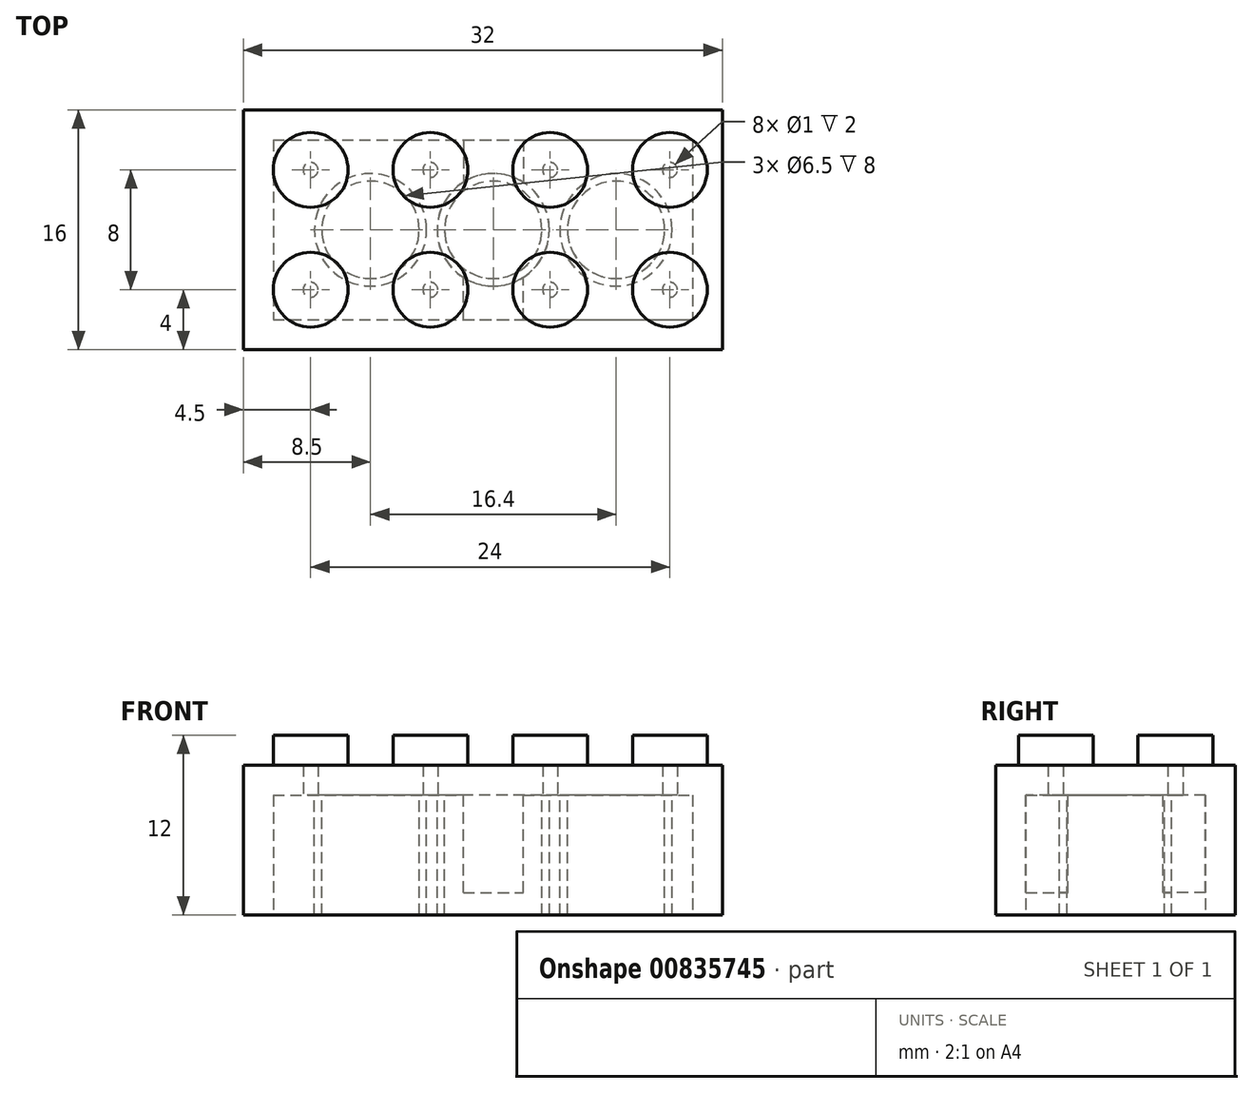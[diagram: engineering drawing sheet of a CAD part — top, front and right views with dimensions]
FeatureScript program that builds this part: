
annotation { "Feature Type Name" : "Feature", "Feature Type Description" : "" }
export const myFeature = defineFeature(function(context is Context, id is Id, definition is map)
    precondition{}
    {
        {
            var Q0;
            Q0=qCreatedBy(makeId("Top.planeOp"),FACE);
            var sketch = newSketch(context, id + "F0", { "sketchPlane" : qUnion([Q0])});
            skLineSegment(sketch, "E0.bottom", {"start": v(-16, 8) * mm, "end": v(16, 8) * mm});
            skLineSegment(sketch, "E0.top", {"start": v(-16, -8) * mm, "end": v(16, -8) * mm});
            skLineSegment(sketch, "E0.left", {"start": v(-16, 8) * mm, "end": v(-16, -8) * mm});
            skLineSegment(sketch, "E0.right", {"start": v(16, 8) * mm, "end": v(16, -8) * mm});
            skPoint(sketch, "E1", {"position": v(-16, 0) * mm});
            skPoint(sketch, "E2", {"position": v(0, 8) * mm});
            skPoint(sketch, "E3", {"position": v(16, 0) * mm});
            skPoint(sketch, "E4", {"position": v(0, -8) * mm});
            skPoint(sketch, "E5", {"position": v(0, 0) * mm});
            skSolve(sketch);
        }
        {
            var Q0;
            Q0=makeQuery(id+"F0.imprint","IMPRINT",FACE,{"disambiguationData":[TD([[makeQuery(id+"F0.imprint","IMPRINT",EDGE,{"derivedFrom":sQuery(id+"F0.wireOp",EDGE,"E0.bottom")}),-1.0]])]});
            extrude(context, id + "F1", {"entities" : qUnion([Q0]), "depth" : 10 * mm, "offsetDistance" : 25 * mm});
        }
        {
            var Q0;
            Q0=makeQuery(id+"F1.opExtrude","CAP_FACE",FACE,{"disambiguationData":[OSD([sQuery(id+"F0.wireOp",EDGE,"E0.bottom"),sQuery(id+"F0.wireOp",EDGE,"E0.top"),sQuery(id+"F0.wireOp",EDGE,"E0.left"),sQuery(id+"F0.wireOp",EDGE,"E0.right")])],"isStart":false});
            var sketch = newSketch(context, id + "F2", { "sketchPlane" : qUnion([Q0])});
            skCircle(sketch, "E6", {"center": v(-11.5, 4) * mm, "radius": 2.5 * mm});
            skCircle(sketch, "E7.0.1.0", {"center": v(-11.5, -4) * mm, "radius": 2.5 * mm});
            skCircle(sketch, "E7.1.0.0", {"center": v(-3.5, 4) * mm, "radius": 2.5 * mm});
            skCircle(sketch, "E7.1.1.0", {"center": v(-3.5, -4) * mm, "radius": 2.5 * mm});
            skCircle(sketch, "E7.2.0.0", {"center": v(4.5, 4) * mm, "radius": 2.5 * mm});
            skCircle(sketch, "E7.2.1.0", {"center": v(4.5, -4) * mm, "radius": 2.5 * mm});
            skCircle(sketch, "E7.3.0.0", {"center": v(12.5, 4) * mm, "radius": 2.5 * mm});
            skCircle(sketch, "E7.3.1.0", {"center": v(12.5, -4) * mm, "radius": 2.5 * mm});
            skLineSegment(sketch, "E7.direction1", {"start": v(-11.5, 4) * mm, "end": v(-3.5, 4) * mm, "construction": true});
            skLineSegment(sketch, "E7.direction2", {"start": v(-11.5, 4) * mm, "end": v(-11.5, -4) * mm, "construction": true});
            skSolve(sketch);
        }
        {
            var Q0;
            Q0=makeQuery(id+"F2.imprint","IMPRINT",FACE,{"disambiguationData":[TD([[makeQuery(id+"F2.imprint","IMPRINT",EDGE,{"derivedFrom":sQuery(id+"F2.wireOp",EDGE,"E6")}),1.0]])]});
            var Q1;
            Q1=makeQuery(id+"F2.imprint","IMPRINT",FACE,{"disambiguationData":[TD([[makeQuery(id+"F2.imprint","IMPRINT",EDGE,{"derivedFrom":sQuery(id+"F2.wireOp",EDGE,"E7.1.0.0")}),1.0]])]});
            var Q2;
            Q2=makeQuery(id+"F2.imprint","IMPRINT",FACE,{"disambiguationData":[TD([[makeQuery(id+"F2.imprint","IMPRINT",EDGE,{"derivedFrom":sQuery(id+"F2.wireOp",EDGE,"E7.3.0.0")}),1.0]])]});
            var Q3;
            Q3=makeQuery(id+"F2.imprint","IMPRINT",FACE,{"disambiguationData":[TD([[makeQuery(id+"F2.imprint","IMPRINT",EDGE,{"derivedFrom":sQuery(id+"F2.wireOp",EDGE,"E7.3.1.0")}),1.0]])]});
            var Q4;
            Q4=makeQuery(id+"F2.imprint","IMPRINT",FACE,{"disambiguationData":[TD([[makeQuery(id+"F2.imprint","IMPRINT",EDGE,{"derivedFrom":sQuery(id+"F2.wireOp",EDGE,"E7.2.1.0")}),1.0]])]});
            var Q5;
            Q5=makeQuery(id+"F2.imprint","IMPRINT",FACE,{"disambiguationData":[TD([[makeQuery(id+"F2.imprint","IMPRINT",EDGE,{"derivedFrom":sQuery(id+"F2.wireOp",EDGE,"E7.1.1.0")}),1.0]])]});
            var Q6;
            Q6=makeQuery(id+"F2.imprint","IMPRINT",FACE,{"disambiguationData":[TD([[makeQuery(id+"F2.imprint","IMPRINT",EDGE,{"derivedFrom":sQuery(id+"F2.wireOp",EDGE,"E7.0.1.0")}),1.0]])]});
            var Q7;
            Q7=makeQuery(id+"F2.imprint","IMPRINT",FACE,{"disambiguationData":[TD([[makeQuery(id+"F2.imprint","IMPRINT",EDGE,{"derivedFrom":sQuery(id+"F2.wireOp",EDGE,"E7.2.0.0")}),1.0]])]});
            extrude(context, id + "F3", {"entities" : qUnion([Q0, Q1, Q2, Q3, Q4, Q5, Q6, Q7]), "operationType" : NewBodyOperationType.ADD, "depth" : 2 * mm, "offsetDistance" : 25 * mm});
        }
        {
            var Q0;
            Q0=makeQuery(id+"F1.opExtrude","CAP_FACE",FACE,{"disambiguationData":[OSD([sQuery(id+"F0.wireOp",EDGE,"E0.bottom"),sQuery(id+"F0.wireOp",EDGE,"E0.top"),sQuery(id+"F0.wireOp",EDGE,"E0.left"),sQuery(id+"F0.wireOp",EDGE,"E0.right")])],"isStart":true});
            shell(context, id + "F4", {"entities" : qUnion([Q0]), "thickness" : 2 * mm});
        }
        {
            var Q0;
            Q0=makeQuery(id+"F4.opShell","OFFSET_FACE",FACE,{"disambiguationData":[OSD([sQuery(id+"F0.wireOp",EDGE,"E0.bottom"),sQuery(id+"F0.wireOp",EDGE,"E0.top"),sQuery(id+"F0.wireOp",EDGE,"E0.left"),sQuery(id+"F0.wireOp",EDGE,"E0.right")])]});
            var sketch = newSketch(context, id + "F5", { "sketchPlane" : qUnion([Q0])});
            skCircle(sketch, "E8", {"center": v(-7.5, 0) * mm, "radius": 3.75 * mm});
            skLineSegment(sketch, "E9", {"start": v(-11.5, 4) * mm, "end": v(-11.5, -4) * mm, "construction": true});
            skLineSegment(sketch, "E10", {"start": v(-11.5, 4) * mm, "end": v(-3.5, 4) * mm, "construction": true});
            skPoint(sketch, "E11", {"position": v(-11.5, 0) * mm});
            skPoint(sketch, "E12", {"position": v(-7.5, 4) * mm});
            skCircle(sketch, "E13", {"center": v(-7.5, 0) * mm, "radius": 3.25 * mm});
            skCircle(sketch, "E14.1.0.0", {"center": v(0.7, 0) * mm, "radius": 3.75 * mm});
            skCircle(sketch, "E14.1.0.1", {"center": v(0.7, 0) * mm, "radius": 3.25 * mm});
            skCircle(sketch, "E14.2.0.0", {"center": v(8.9, 0) * mm, "radius": 3.75 * mm});
            skCircle(sketch, "E14.2.0.1", {"center": v(8.9, 0) * mm, "radius": 3.25 * mm});
            skLineSegment(sketch, "E14.direction1", {"start": v(-7.5, 0) * mm, "end": v(0.7, 0) * mm, "construction": true});
            skSolve(sketch);
        }
        {
            var Q0;
            Q0=makeQuery(id+"F5.imprint","IMPRINT",FACE,{"disambiguationData":[TD([[makeQuery(id+"F5.imprint","IMPRINT",EDGE,{"derivedFrom":sQuery(id+"F5.wireOp",EDGE,"E8")}),1.0]])]});
            var Q1;
            Q1=makeQuery(id+"F5.imprint","IMPRINT",FACE,{"disambiguationData":[TD([[makeQuery(id+"F5.imprint","IMPRINT",EDGE,{"derivedFrom":sQuery(id+"F5.wireOp",EDGE,"E14.1.0.0")}),1.0]])]});
            var Q2;
            Q2=makeQuery(id+"F5.imprint","IMPRINT",FACE,{"disambiguationData":[TD([[makeQuery(id+"F5.imprint","IMPRINT",EDGE,{"derivedFrom":sQuery(id+"F5.wireOp",EDGE,"E14.2.0.0")}),1.0]])]});
            var Q3;
            Q3=makeQuery(id+"F1.opExtrude","CAP_FACE",FACE,{"disambiguationData":[OSD([sQuery(id+"F0.wireOp",EDGE,"E0.bottom"),sQuery(id+"F0.wireOp",EDGE,"E0.top"),sQuery(id+"F0.wireOp",EDGE,"E0.left"),sQuery(id+"F0.wireOp",EDGE,"E0.right")])],"isStart":true});
            extrude(context, id + "F6", {"entities" : qUnion([Q0, Q1, Q2]), "operationType" : NewBodyOperationType.ADD, "endBound" : BoundingType.UP_TO_SURFACE, "depth" : 12 * mm, "endBoundEntityFace" : qUnion([Q3]), "offsetDistance" : 25 * mm});
        }
        {
            var Q0;
            {var subQ4=sQuery(id+"F0.wireOp",EDGE,"E0.bottom");var subQ6=sQuery(id+"F0.wireOp",EDGE,"E0.top");var subQ7=sQuery(id+"F0.wireOp",EDGE,"E0.left");var subQ9=sQuery(id+"F0.wireOp",EDGE,"E0.right");Q0=makeQuery(id+"F6.boolean.opBoolean","SPLIT",FACE,{"disambiguationData":[TD([makeQuery(id+"F4.opShell","OFFSET_FACE",FACE,{"disambiguationData":[OSD([subQ4])]})])],"derivedFrom":makeQuery(id+"F4.opShell","OFFSET_FACE",FACE,{"disambiguationData":[OSD([subQ4,subQ6,subQ7,subQ9])]})});}
            var sketch = newSketch(context, id + "F7", { "sketchPlane" : qUnion([Q0])});
            skCircle(sketch, "E15.0", {"center": v(0.7, 0) * mm, "radius": 3.75 * mm});
            skLineSegment(sketch, "E16", {"start": v(0.7, 9.8) * mm, "end": v(0.7, -11.34) * mm, "construction": true});
            skLineSegment(sketch, "E17", {"start": v(-1.3, 6) * mm, "end": v(-1.3, 3.17) * mm});
            skLineSegment(sketch, "E18", {"start": v(2.7, 6) * mm, "end": v(2.7, 3.17) * mm});
            skLineSegment(sketch, "E19", {"start": v(-1.3, -6) * mm, "end": v(-1.3, -3.17) * mm});
            skLineSegment(sketch, "E20", {"start": v(2.7, -6) * mm, "end": v(2.7, -3.17) * mm});
            skSolve(sketch);
        }
        {
            var Q0;
            {var subQ0=sQuery(id+"F7.wireOp",EDGE,"E17");Q0=makeQuery(id+"F7.imprint","IMPRINT",FACE,{"disambiguationData":[TD([[makeQuery(id+"F7.imprint","IMPRINT",EDGE,{"derivedFrom":subQ0}),1.0]])]});}
            var Q1;
            {var subQ0=sQuery(id+"F7.wireOp",EDGE,"E19");Q1=makeQuery(id+"F7.imprint","IMPRINT",FACE,{"disambiguationData":[TD([[makeQuery(id+"F7.imprint","IMPRINT",EDGE,{"derivedFrom":subQ0}),-1.0]])]});}
            extrude(context, id + "F8", {"entities" : qUnion([Q0, Q1]), "operationType" : NewBodyOperationType.ADD, "depth" : 6.5 * mm, "offsetDistance" : 25 * mm});
        }
    });
